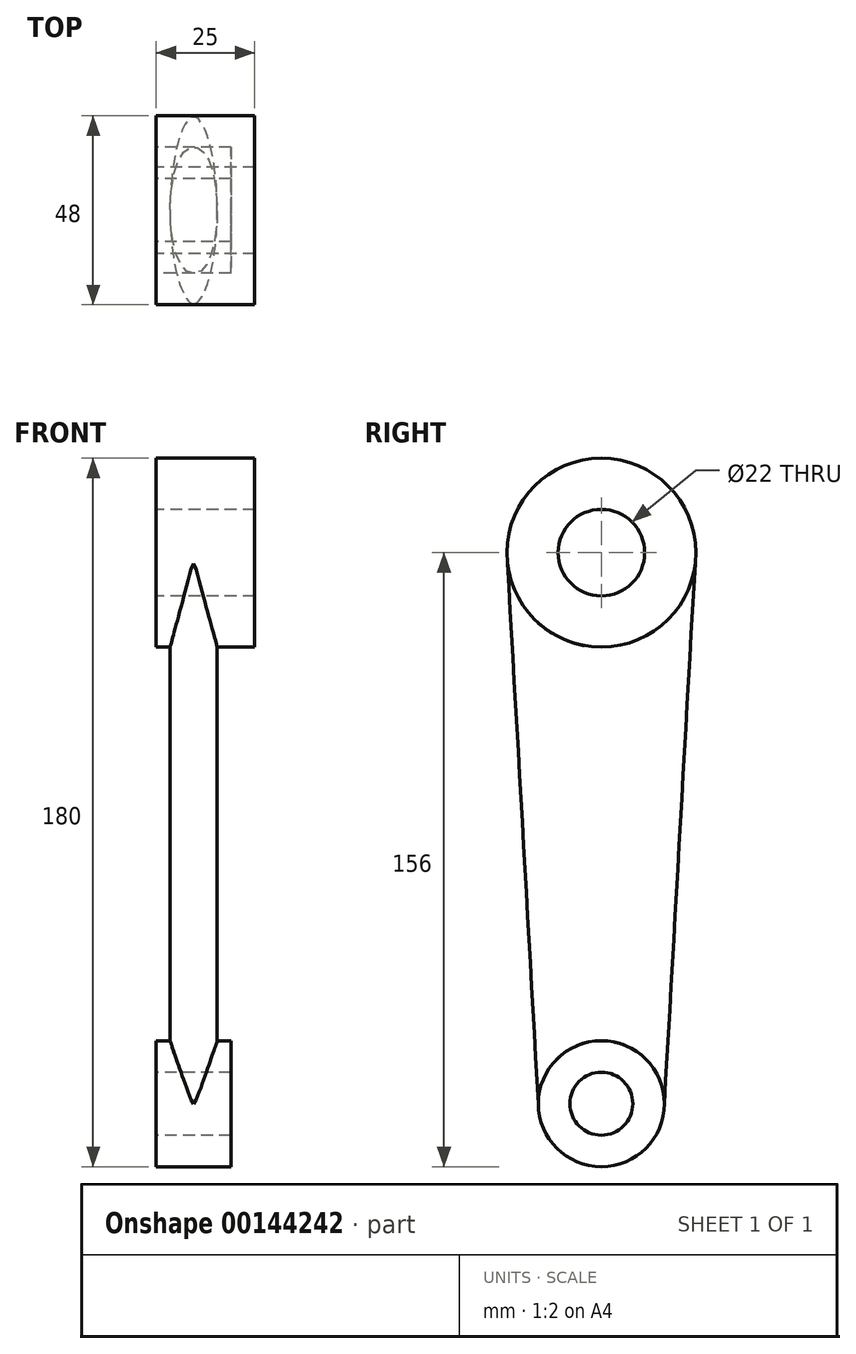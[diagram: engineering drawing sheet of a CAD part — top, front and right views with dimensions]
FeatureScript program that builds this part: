
annotation { "Feature Type Name" : "Feature", "Feature Type Description" : "" }
export const myFeature = defineFeature(function(context is Context, id is Id, definition is map)
    precondition{}
    {
        {
            var Q0;
            Q0=qCreatedBy(makeId("Right.planeOp"),FACE);
            var sketch = newSketch(context, id + "F0", { "sketchPlane" : qUnion([Q0])});
            skCircle(sketch, "E0", {"center": v(0, 0) * mm, "radius": 8 * mm});
            skCircle(sketch, "E1", {"center": v(0, 140) * mm, "radius": 11 * mm});
            skCircle(sketch, "E2", {"center": v(0, 140) * mm, "radius": 24 * mm});
            skCircle(sketch, "E3", {"center": v(0, 0) * mm, "radius": 16 * mm});
            skSolve(sketch);
        }
        {
            var Q0;
            Q0=makeQuery(id+"F0.imprint","IMPRINT",FACE,{"disambiguationData":[TD([[makeQuery(id+"F0.imprint","IMPRINT",EDGE,{"derivedFrom":sQuery(id+"F0.wireOp",EDGE,"E1")}),-1.0]])]});
            var Q1;
            Q1=makeQuery(id+"F0.imprint","IMPRINT",FACE,{"disambiguationData":[TD([[makeQuery(id+"F0.imprint","IMPRINT",EDGE,{"derivedFrom":sQuery(id+"F0.wireOp",EDGE,"E1")}),1.0]])]});
            extrude(context, id + "F1", {"entities" : qUnion([Q0, Q1]), "depth" : 25 * mm});
        }
        {
            var Q0;
            Q0=makeQuery(id+"F0.imprint","IMPRINT",FACE,{"disambiguationData":[TD([[makeQuery(id+"F0.imprint","IMPRINT",EDGE,{"derivedFrom":sQuery(id+"F0.wireOp",EDGE,"E0")}),-1.0]])]});
            var Q1;
            Q1=makeQuery(id+"F0.imprint","IMPRINT",FACE,{"disambiguationData":[TD([[makeQuery(id+"F0.imprint","IMPRINT",EDGE,{"derivedFrom":sQuery(id+"F0.wireOp",EDGE,"E0")}),1.0]])]});
            extrude(context, id + "F2", {"entities" : qUnion([Q0, Q1]), "depth" : 19 * mm});
        }
        {
            var Q0;
            Q0=qCreatedBy(makeId("Top.planeOp"),FACE);
            var sketch = newSketch(context, id + "F3", { "sketchPlane" : qUnion([Q0])});
            skEllipse(sketch, "E4", {"center": v(9.5, 0) * mm, "majorRadius": 16 * mm, "minorRadius": 6 * mm, "majorAxis": v(0, 1)});
            skPoint(sketch, "E5", {"position": v(3.5, 0) * mm});
            skPoint(sketch, "E6", {"position": v(15.5, 0) * mm});
            skLineSegment(sketch, "E7", {"start": v(0, 16) * mm, "end": v(19, 16) * mm, "construction": true});
            skSolve(sketch);
        }
        {
            var Q0;
            Q0=sQuery(id+"F0.wireOp",VERTEX,"E2.center");
            var Q1;
            Q1=qCreatedBy(makeId("Top.planeOp"),FACE);
            cPlane(context, id + "F4", {"entities" : qUnion([Q0, Q1]), "cplaneType" : CPlaneType.PLANE_POINT, "offset" : 25 * mm, "width" : 150 * mm, "height" : 150 * mm});
        }
        {
            var Q0;
            Q0=qCreatedBy(id+"F4.planeOp",FACE);
            var sketch = newSketch(context, id + "F5", { "sketchPlane" : qUnion([Q0])});
            skEllipse(sketch, "E8", {"center": v(9.5, 0) * mm, "majorRadius": 24 * mm, "minorRadius": 6 * mm, "majorAxis": v(0, -1)});
            skPoint(sketch, "E9", {"position": v(3.5, 0) * mm});
            skLineSegment(sketch, "E10", {"start": v(0, 24) * mm, "end": v(25, 24) * mm, "construction": true});
            skSolve(sketch);
        }
        {
            var Q0;
            Q0=makeQuery(id+"F5.imprint","IMPRINT",FACE,{"disambiguationData":[TD([[makeQuery(id+"F5.imprint","IMPRINT",EDGE,{"derivedFrom":sQuery(id+"F5.wireOp",EDGE,"E8")}),1.0]])]});
            var Q1;
            Q1 = qSketchRegion(id + "F3", true);
            loft(context, id + "F6", {"operationType" : NewBodyOperationType.ADD, "sheetProfilesArray" : [{ "sheetProfileEntities" : qUnion([Q0]) }, { "sheetProfileEntities" : qUnion([Q1]) }]});
        }
        {
            var Q0;
            Q0=makeQuery(id+"F0.imprint","IMPRINT",FACE,{"disambiguationData":[TD([[makeQuery(id+"F0.imprint","IMPRINT",EDGE,{"derivedFrom":sQuery(id+"F0.wireOp",EDGE,"E0")}),1.0]])]});
            extrude(context, id + "F7", {"entities" : qUnion([Q0]), "operationType" : NewBodyOperationType.REMOVE, "endBound" : BoundingType.THROUGH_ALL, "depth" : 25 * mm});
        }
        {
            var Q0;
            Q0=makeQuery(id+"F0.imprint","IMPRINT",FACE,{"disambiguationData":[TD([[makeQuery(id+"F0.imprint","IMPRINT",EDGE,{"derivedFrom":sQuery(id+"F0.wireOp",EDGE,"E1")}),1.0]])]});
            extrude(context, id + "F8", {"entities" : qUnion([Q0]), "operationType" : NewBodyOperationType.REMOVE, "endBound" : BoundingType.THROUGH_ALL, "depth" : 25 * mm});
        }
    });
